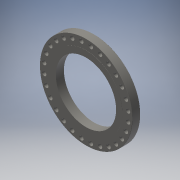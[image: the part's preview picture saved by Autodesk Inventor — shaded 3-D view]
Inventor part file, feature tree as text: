
AUTODESK INVENTOR PART (.ipt)
format: ipt  version: 2017 SP1 (Build 210196100, 196)  size: 286,720 bytes
history: native  units: in
note: dims shown in document units (in); Inventor stores cm internally (conversion verified against a paired STEP export)
features: sketch x6, extrude x4, chamfer x3, hole x2, pattern_circular x2, fillet x1, plane x1, projected_geometry x1
ambient origin geometry x8: Origin, YZ Plane, XZ Plane, XY Plane, X Axis, Y Axis, Z Axis, Center Point
bodies: Solid1 (feature_tree)
feature tree (20):
  extrude  "Extrusion: OD"  Depth=3.6875in TaperAngle=0.0deg
  extrude  "Extrusion: RF"  Depth=0.0625in TaperAngle=0.0deg
  extrude  "Extrusion: ID Large"  Depth=2.0in TaperAngle=0.0deg
  extrude  "Extrusion: ID Small"  Depth=2.0in TaperAngle=0.0deg
  hole  "Hole: Bolt"  [1 undecoded]
  chamfer  "Chamfer: Bolt hole"  Distance=11.0236in Angle=360.0deg
  pattern_circular  "Circular Pattern: Bolt hole"  Angle=45.0deg  [1 undecoded]
  chamfer  "Chamfer: OD"  Distance=0.0312in Angle=45.0deg
  chamfer  "Chamfer2"  Distance=0.0312in
  fillet  "Fillet2"  Radius=0.25in
  plane  "Work Plane1"
  hole  "Hole2"  [1 undecoded]
  pattern_circular  "Circular Pattern2"  [2 undecoded]
  sketch  "Sketch1"  dims[d0=43.0in d1=3.6875in d2=0.0in]
  sketch  "Sketch2"  dims[d3=33.75in d4=0.0625in d5=0.0in]
  sketch  "Sketch3"  dims[d6=30.0in d7=2.0in d8=0.0in]
  sketch  "Sketch4"  dims[d9=28.0in d10=2.0in d11=0.0in]
  sketch  "Sketch5"  dims[d12=39.25in d13=0.0442in]
  sketch  "Sketch6"  dims[d14=1.875in d15=0.75in d16=0.375in d17=0.25in d18=0.5635in d19=1.0in d20=0.8108in d21=11.0236in d22=360.0deg d24=0.0625in d25=0.125in d26=45.0deg d28=0.0312in d29=0.125in d30=45.0deg d31=0.0312in d32=0.25in d33=0.0625in d34=0.125in d35=45.0deg d36=1.875in d37=0.642in d38=2.0in d39=0.375in d40=0.25in d41=0.5635in d42=2.5in d43=0.8108in d44=0.7874in d45=360.0deg]
  projected_geometry  "Projected Loop1"
note: 5 required parameter values undecoded (feature->parameter linkage not recoverable at this tier; creation-order binding heuristic only, values carry confidence <= 0.55)
